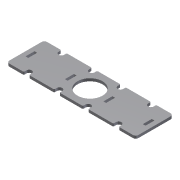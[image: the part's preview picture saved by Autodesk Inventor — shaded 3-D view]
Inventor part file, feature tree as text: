
AUTODESK INVENTOR PART (.ipt)
format: ipt  version: 2012 (Build 160160000, 160)  size: 189,440 bytes
history: native  units: mm
features: extrude x1, sketch x1
ambient origin geometry x8: Origin, YZ Plane, XZ Plane, XY Plane, X Axis, Y Axis, Z Axis, Center Point
feature tree (2):
  extrude  "Extrusion4"  Depth=20.0mm
  sketch  "Sketch1"  dims[d0=10.0mm d1=20.0mm d3=140.0mm d5=3.0mm d6=3.0mm d7=28.0mm d12=50.0mm d13=72.0mm d16=5.0mm d17=3.0mm d18=3.0mm d19=10.0mm d20=3.0mm d21=10.0mm d22=20.0mm d23=20.0mm d24=20.0mm d25=20.0mm d28=5.0mm d29=3.0mm d30=10.0mm d31=20.0mm d34=3.0mm d35=0.0mm d43=6.0mm d45=6.0mm d47=16.0mm d48=16.0mm d49=5.0mm d50=5.0mm d51=5.0mm d52=5.0mm d53=6.0mm d54=3.0mm d55=100.0mm d56=50.0mm d57=1.0mm d58=42.0mm d59=21.0mm d61=16.0mm d62=16.0mm d63=2.0mm d64=2.0mm d65=2.0mm d66=2.0mm d67=1.0mm d68=144.0mm d69=50.0mm d70=3.0mm d71=3.0mm d72=3.0mm d73=3.0mm d74=3.0mm d75=3.0mm d76=3.0mm]
